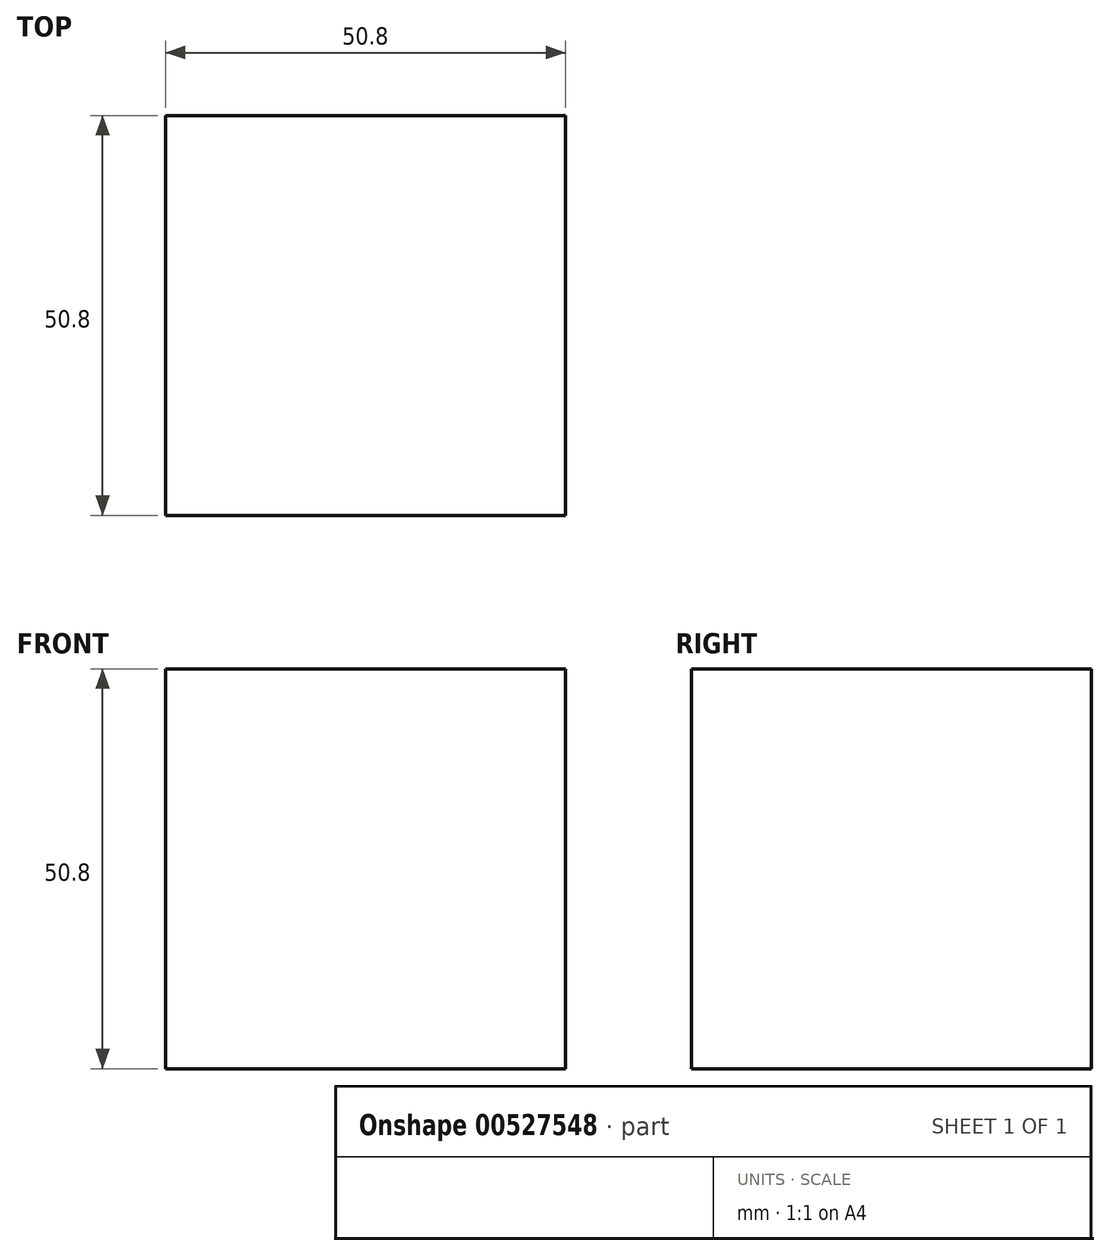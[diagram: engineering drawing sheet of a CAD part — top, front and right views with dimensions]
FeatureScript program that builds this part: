
annotation { "Feature Type Name" : "Feature", "Feature Type Description" : "" }
export const myFeature = defineFeature(function(context is Context, id is Id, definition is map)
    precondition{}
    {
        {
            var Q0;
            Q0=qCreatedBy(makeId("Front.planeOp"),FACE);
            var sketch = newSketch(context, id + "F0", { "sketchPlane" : qUnion([Q0])});
            skLineSegment(sketch, "E0", {"start": v(0, 0) * mm, "end": v(50.8, 0) * mm});
            skLineSegment(sketch, "E1", {"start": v(50.8, 50.8) * mm, "end": v(0, 50.8) * mm});
            skLineSegment(sketch, "E2", {"start": v(0, 50.8) * mm, "end": v(0, 0) * mm});
            skLineSegment(sketch, "E3", {"start": v(50.8, 50.8) * mm, "end": v(50.8, 0) * mm});
            skSolve(sketch);
        }
        {
            var Q0;
            Q0=makeQuery(id+"F0.imprint","IMPRINT",FACE,{"disambiguationData":[TD([[makeQuery(id+"F0.imprint","IMPRINT",EDGE,{"derivedFrom":sQuery(id+"F0.wireOp",EDGE,"E0")}),1.0]])]});
            extrude(context, id + "F1", {"entities" : qUnion([Q0]), "depth" : 50.8 * mm, "offsetDistance" : 25.4 * mm});
        }
    });
